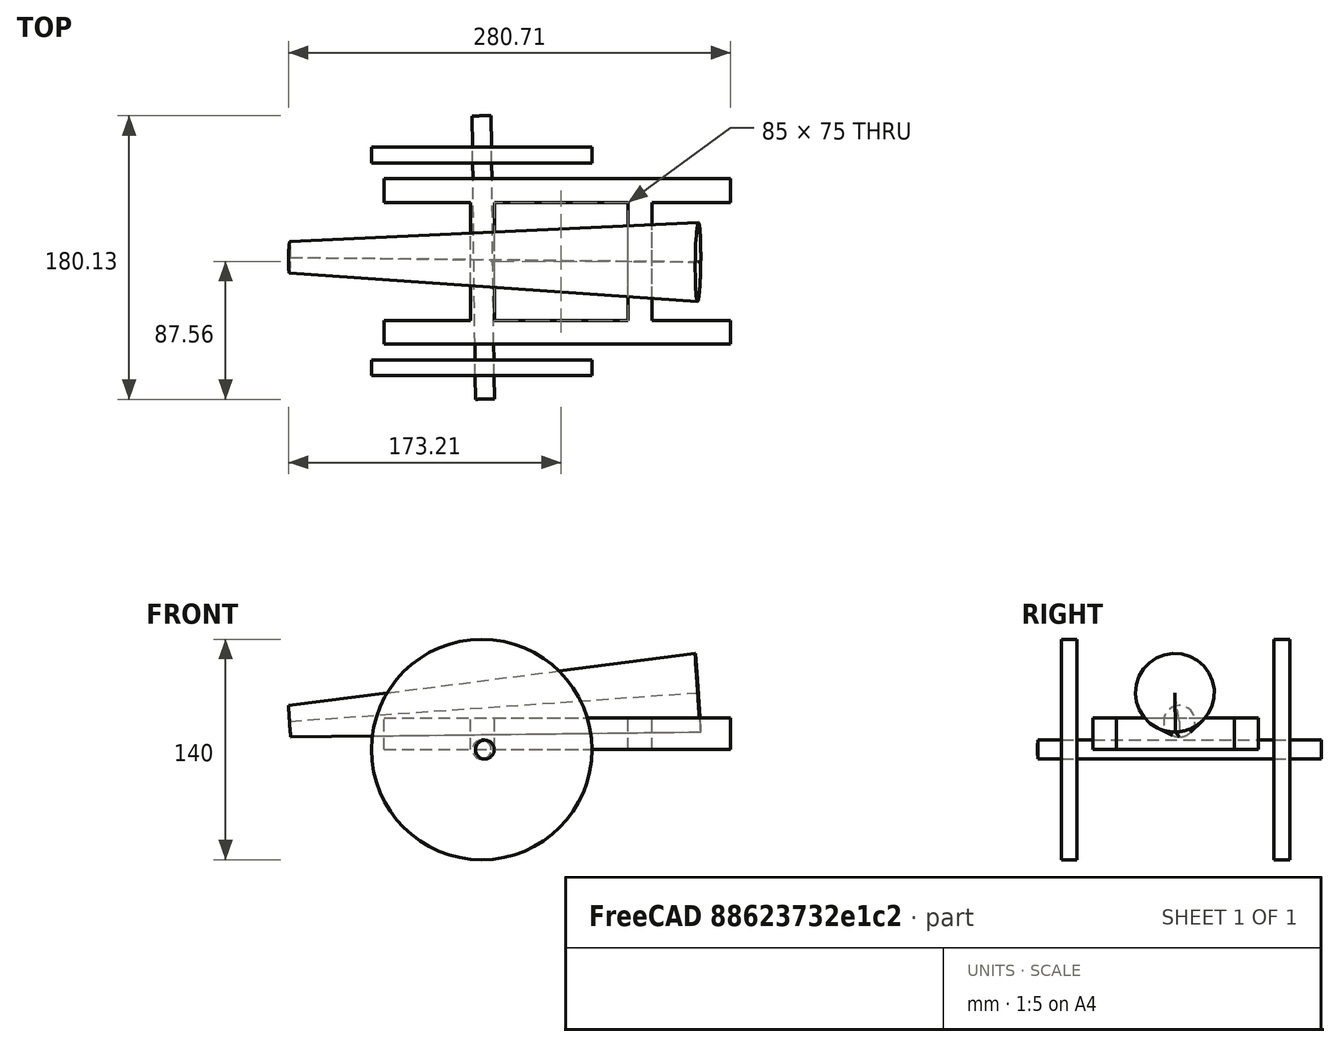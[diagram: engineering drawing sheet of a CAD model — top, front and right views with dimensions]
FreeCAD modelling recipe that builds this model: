
FCSTD DOCUMENT  (FreeCAD 1.0R38806 (Git))
Label: Cañon
License: All rights reserved
LicenseURL: http://en.wikipedia.org/wiki/All_rights_reserved
objects: Part::Box×4, Part::Cylinder×3, Part::MultiFuse×1, Part::Cone×1
note: 9 computed .brp shape members not serialized (recipe doc carries the construction recipe); baked Part::Feature solids carry a one-line shape summary decoded from their .brp

FEATURE [Part::Box] Box  label="Estructura1"
  AttacherType = Attacher::AttachEngine3D
  Height = 20
  Length = 15
  Width = 100
FEATURE [Part::Box] Box001  label="Estructura2"
  AttacherType = Attacher::AttachEngine3D
  Height = 20
  Length = 15
  Placement = pos=(100,0,0) rot=(0,0,1;0rad)
  Width = 100
FEATURE [Part::Box] Box002  label="Estructura3"
  AttacherType = Attacher::AttachEngine3D
  Height = 20
  Length = 220
  Placement = pos=(-55,0,0) rot=(0,0,1;0rad)
  Width = 15
FEATURE [Part::Box] Box003  label="Estructura4"
  AttacherType = Attacher::AttachEngine3D
  Height = 20
  Length = 220
  Placement = pos=(-55,90,0) rot=(0,0,1;0rad)
  Width = 15
FEATURE [Part::MultiFuse] Fusion  label="Estructura"
  Refine = true
  Shapes = -> [Box,Box001,Box002,Box003]
FEATURE [Part::Cylinder] Cylinder  label="Eje"
  Angle = 360
  AttacherType = Attacher::AttachEngine3D
  FirstAngle = 0
  Height = 180
  Placement = pos=(7,145,0) rot=(90,1,0;1.5708rad)
  Radius = 6
  SecondAngle = 0
FEATURE [Part::Cone] Cone  label="Cono"
  Angle = 360
  AttacherType = Attacher::AttachEngine3D
  Height = 260
  Placement = pos=(-115,55,18) rot=(1,90,0;1.50098rad)
  Radius1 = 10
  Radius2 = 25
FEATURE [Part::Cylinder] Cylinder001  label="Rueda1"
  Angle = 360
  AttacherType = Attacher::AttachEngine3D
  FirstAngle = 0
  Height = 10
  Placement = pos=(7,-10,0) rot=(1,0,0;1.5708rad)
  Radius = 70
  SecondAngle = 0
FEATURE [Part::Cylinder] Cylinder002  label="Rueda2"
  Angle = 360
  AttacherType = Attacher::AttachEngine3D
  FirstAngle = 0
  Height = 10
  Placement = pos=(7,125,0) rot=(1,0,0;1.5708rad)
  Radius = 70
  SecondAngle = 0
